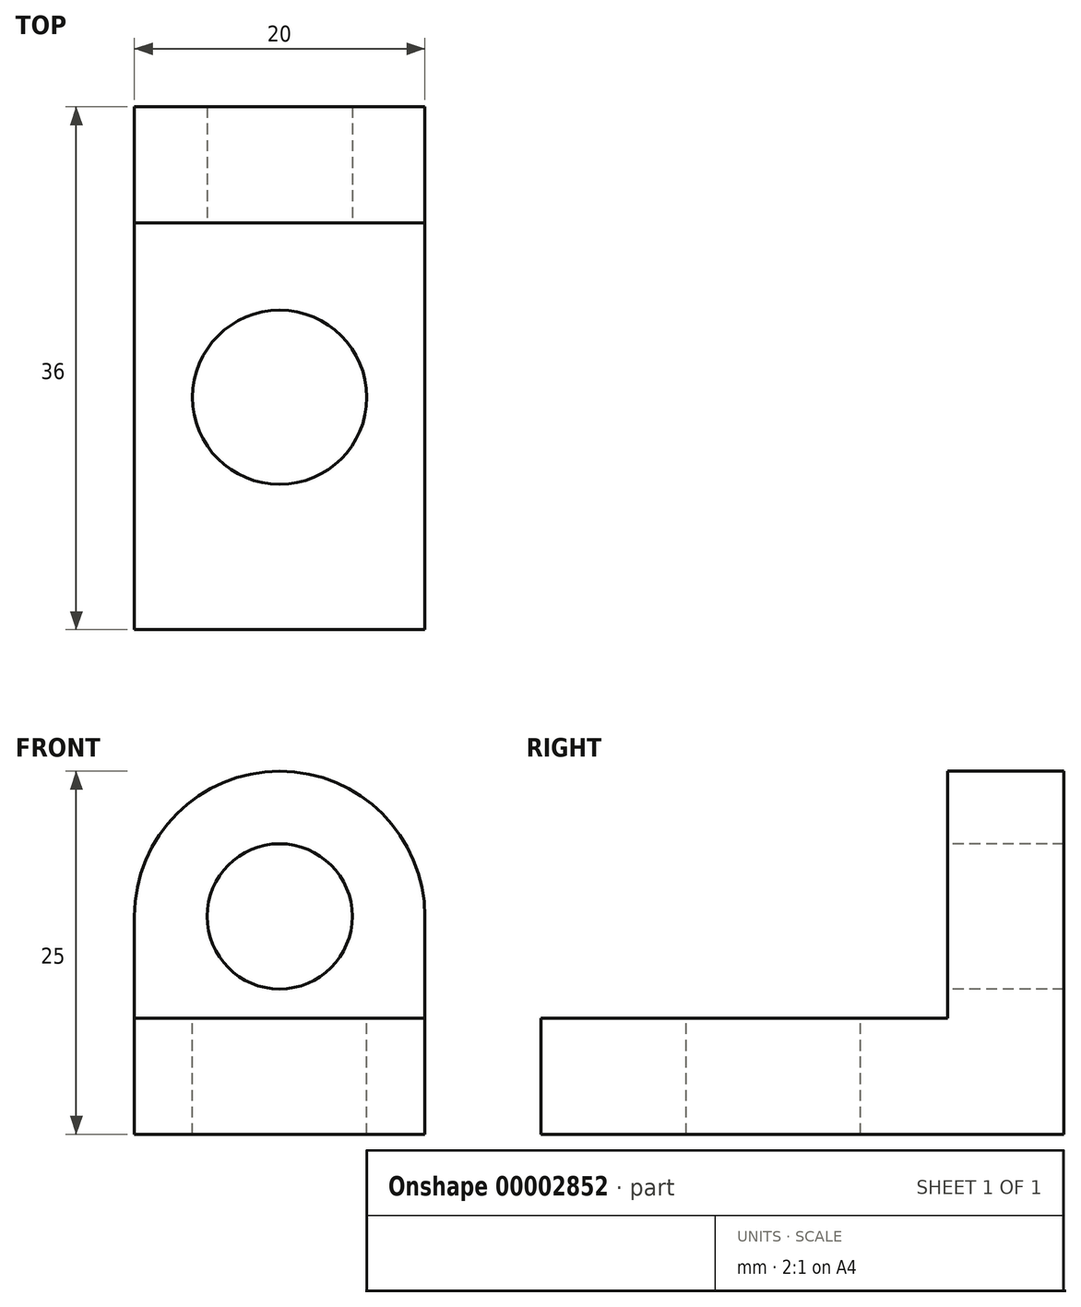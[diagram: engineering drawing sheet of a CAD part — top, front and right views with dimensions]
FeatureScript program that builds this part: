
annotation { "Feature Type Name" : "Feature", "Feature Type Description" : "" }
export const myFeature = defineFeature(function(context is Context, id is Id, definition is map)
    precondition{}
    {
        {
            var Q0;
            Q0=qCreatedBy(makeId("Top.planeOp"),FACE);
            var sketch = newSketch(context, id + "F0", { "sketchPlane" : qUnion([Q0])});
            skLineSegment(sketch, "E0", {"start": v(0, 0) * mm, "end": v(10, 0) * mm});
            skLineSegment(sketch, "E1", {"start": v(10, 0) * mm, "end": v(10, -28) * mm});
            skLineSegment(sketch, "E2", {"start": v(10, -28) * mm, "end": v(0, -28) * mm});
            skLineSegment(sketch, "E3.0.MirrorCS", {"start": v(-10, 0) * mm, "end": v(-10, -28) * mm});
            skLineSegment(sketch, "E4.0.MirrorCS", {"start": v(-10, -28) * mm, "end": v(0, -28) * mm});
            skLineSegment(sketch, "E5.0.MirrorCS", {"start": v(0, 0) * mm, "end": v(-10, 0) * mm});
            skSolve(sketch);
        }
        {
            var Q0;
            Q0 = qSketchRegion(id + "F0", true);
            extrude(context, id + "F1", {"entities" : qUnion([Q0]), "depth" : 8 * mm});
        }
        {
            var Q0;
            Q0=makeQuery(id+"F1.opExtrude","SWEPT_FACE",FACE,{"disambiguationData":[OSD([sQuery(id+"F0.wireOp",EDGE,"E0")])]});
            var sketch = newSketch(context, id + "F2", { "sketchPlane" : qUnion([Q0])});
            skLineSegment(sketch, "E6.bottom", {"start": v(0, 0) * mm, "end": v(10, 0) * mm});
            skLineSegment(sketch, "E6.top", {"start": v(0, 15) * mm, "end": v(10, 15) * mm});
            skLineSegment(sketch, "E6.right", {"start": v(10, 0) * mm, "end": v(10, 15) * mm});
            skLineSegment(sketch, "E7.0.MirrorCS", {"start": v(0, 15) * mm, "end": v(-10, 15) * mm});
            skLineSegment(sketch, "E8.0.MirrorCS", {"start": v(-10, 0) * mm, "end": v(-10, 15) * mm});
            skLineSegment(sketch, "E9.0.MirrorCS", {"start": v(0, 0) * mm, "end": v(-10, 0) * mm});
            skArc(sketch, "E10", {"start": v(10, 15) * mm, "mid": v(0, 25) * mm, "end": v(-10, 15) * mm});
            skSolve(sketch);
        }
        {
            var Q0;
            {var subQ1=sQuery(id+"F2.wireOp",EDGE,"E6.top");Q0=makeQuery(id+"F2.imprint","IMPRINT",FACE,{"disambiguationData":[TD([[makeQuery(id+"F2.imprint","IMPRINT",EDGE,{"derivedFrom":subQ1}),-1.0]])]});}
            var Q1;
            {var subQ2=sQuery(id+"F2.wireOp",EDGE,"E6.bottom");Q1=makeQuery(id+"F2.imprint","IMPRINT",FACE,{"disambiguationData":[TD([[makeQuery(id+"F2.imprint","IMPRINT",EDGE,{"derivedFrom":subQ2}),-1.0]])]});}
            extrude(context, id + "F3", {"entities" : qUnion([Q0, Q1]), "operationType" : NewBodyOperationType.ADD, "depth" : 8 * mm});
        }
        {
            var Q0;
            Q0=makeQuery(id+"F2.imprint","IMPRINT",FACE,{"disambiguationData":[TD([[makeQuery(id+"F2.imprint","IMPRINT",EDGE,{"derivedFrom":sQuery(id+"F2.wireOp",EDGE,"E6.top")}),1.0]])]});
            extrude(context, id + "F4", {"entities" : qUnion([Q0]), "operationType" : NewBodyOperationType.ADD, "depth" : 8 * mm});
        }
        {
            var Q0;
            Q0=makeQuery(id+"F2.imprint","IMPRINT",FACE,{"disambiguationData":[TD([[makeQuery(id+"F2.imprint","IMPRINT",EDGE,{"derivedFrom":sQuery(id+"F2.wireOp",EDGE,"E6.top")}),1.0]])]});
            var sketch = newSketch(context, id + "F5", { "sketchPlane" : qUnion([Q0])});
            skCircle(sketch, "E11", {"center": v(0, 15) * mm, "radius": 5 * mm});
            skSolve(sketch);
        }
        {
            var Q0;
            {var subQ1=sQuery(id+"F5.wireOp",EDGE,"E11");var subQ3=makeQuery(id+"F2.imprint","IMPRINT",EDGE,{"derivedFrom":sQuery(id+"F2.wireOp",EDGE,"E6.top")});var subQ5=makeQuery(id+"F5.imprint","INTERSECT",VERTEX,{"derivedFrom":[subQ3,subQ1]});Q0=makeQuery(id+"F5.imprint","IMPRINT",FACE,{"disambiguationData":[TD([[makeQuery(id+"F5.imprint","IMPRINT",EDGE,{"disambiguationData":[TD([[subQ5,-1.0]])],"derivedFrom":subQ1}),1.0]])]});}
            var Q1;
            {var subQ1=sQuery(id+"F5.wireOp",EDGE,"E11");var subQ3=makeQuery(id+"F2.imprint","IMPRINT",EDGE,{"derivedFrom":sQuery(id+"F2.wireOp",EDGE,"E6.top")});var subQ5=makeQuery(id+"F5.imprint","INTERSECT",VERTEX,{"derivedFrom":[subQ3,subQ1]});Q1=makeQuery(id+"F5.imprint","IMPRINT",FACE,{"disambiguationData":[TD([[makeQuery(id+"F5.imprint","IMPRINT",EDGE,{"disambiguationData":[TD([[subQ5,1.0]])],"derivedFrom":subQ1}),1.0]])]});}
            extrude(context, id + "F6", {"entities" : qUnion([Q0, Q1]), "operationType" : NewBodyOperationType.REMOVE, "depth" : 8 * mm});
        }
        {
            var Q0;
            Q0=makeQuery(id+"F1.opExtrude","CAP_FACE",FACE,{"disambiguationData":[OSD([sQuery(id+"F0.wireOp",EDGE,"E0"),sQuery(id+"F0.wireOp",EDGE,"E1"),sQuery(id+"F0.wireOp",EDGE,"E3.0.MirrorCS"),sQuery(id+"F0.wireOp",EDGE,"E4.0.MirrorCS")])],"isStart":false});
            var sketch = newSketch(context, id + "F7", { "sketchPlane" : qUnion([Q0])});
            skCircle(sketch, "E12", {"center": v(0, -12) * mm, "radius": 6 * mm});
            skSolve(sketch);
        }
        {
            var Q0;
            Q0=makeQuery(id+"F7.imprint","IMPRINT",FACE,{"disambiguationData":[TD([[makeQuery(id+"F7.imprint","IMPRINT",EDGE,{"derivedFrom":sQuery(id+"F7.wireOp",EDGE,"E12")}),1.0]])]});
            var Q1;
            Q1=sQuery(id+"F7.wireOp",EDGE,"E12");
            extrude(context, id + "F8", {"entities" : qUnion([Q0]), "operationType" : NewBodyOperationType.REMOVE, "surfaceEntities" : qUnion([Q1]), "oppositeDirection" : true, "depth" : 25 * mm});
        }
    });
